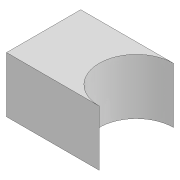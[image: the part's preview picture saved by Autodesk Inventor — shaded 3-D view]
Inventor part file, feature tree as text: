
AUTODESK INVENTOR PART (.ipt)
format: ipt  version: 2022 (Build 260153000, 153)  size: 82,432 bytes
history: native  units: mm
features: extrude x1, sketch x1
ambient origin geometry x8: Origin, YZ Plane, XZ Plane, XY Plane, X Axis, Y Axis, Z Axis, Center Point
bodies: Solid1 (feature_tree)
feature tree (2):
  extrude  "Extrusion1"  Depth=8.0mm
  sketch  "Sketch1"  dims[d2=6.0mm d3=0.0mm d4=8.0mm d5=10.0mm d6=8.0mm]
